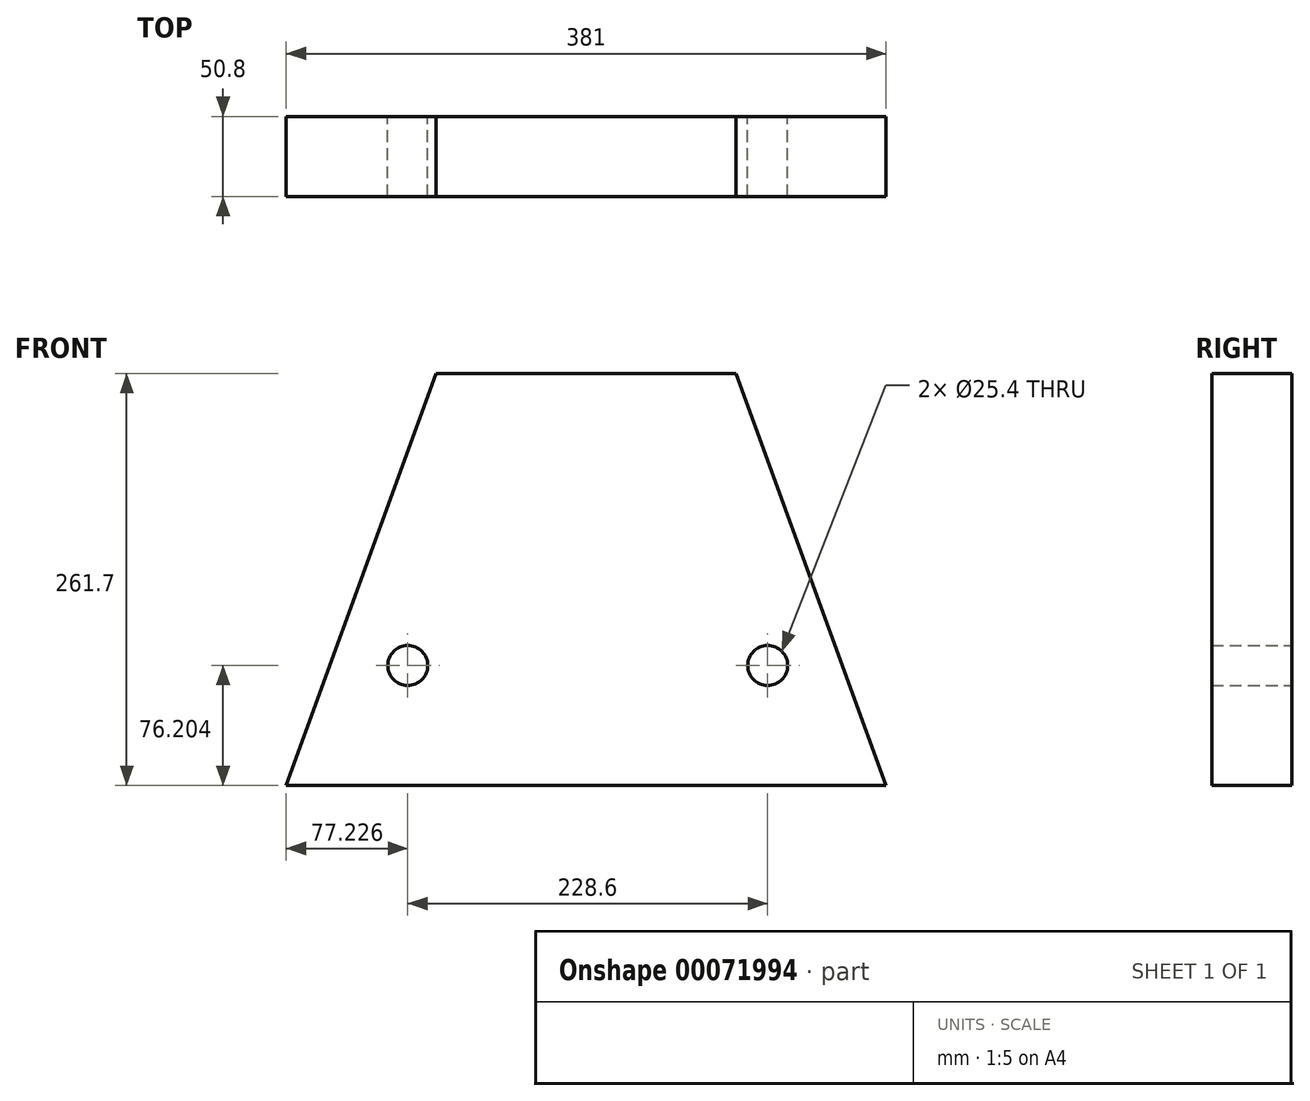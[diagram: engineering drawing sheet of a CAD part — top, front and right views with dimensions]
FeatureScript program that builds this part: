
annotation { "Feature Type Name" : "Feature", "Feature Type Description" : "" }
export const myFeature = defineFeature(function(context is Context, id is Id, definition is map)
    precondition{}
    {
        {
            var Q0;
            Q0=qCreatedBy(makeId("Front.planeOp"),FACE);
            var sketch = newSketch(context, id + "F0", { "sketchPlane" : qUnion([Q0])});
            skLineSegment(sketch, "E0", {"start": v(-231.46, -106.38) * mm, "end": v(149.54, -106.38) * mm});
            skLineSegment(sketch, "E1", {"start": v(-231.46, -106.38) * mm, "end": v(-136.21, 155.32) * mm});
            skLineSegment(sketch, "E2", {"start": v(-136.21, 155.32) * mm, "end": v(54.29, 155.32) * mm});
            skLineSegment(sketch, "E3", {"start": v(54.29, 155.32) * mm, "end": v(149.54, -106.38) * mm});
            skCircle(sketch, "E4", {"center": v(-154.23, -30.18) * mm, "radius": 12.7 * mm});
            skCircle(sketch, "E5", {"center": v(74.37, -30.18) * mm, "radius": 12.7 * mm});
            skSolve(sketch);
        }
        {
            var Q0;
            Q0 = qSketchRegion(id + "F0", true);
            extrude(context, id + "F1", {"entities" : qUnion([Q0]), "depth" : 50.8 * mm});
        }
    });
